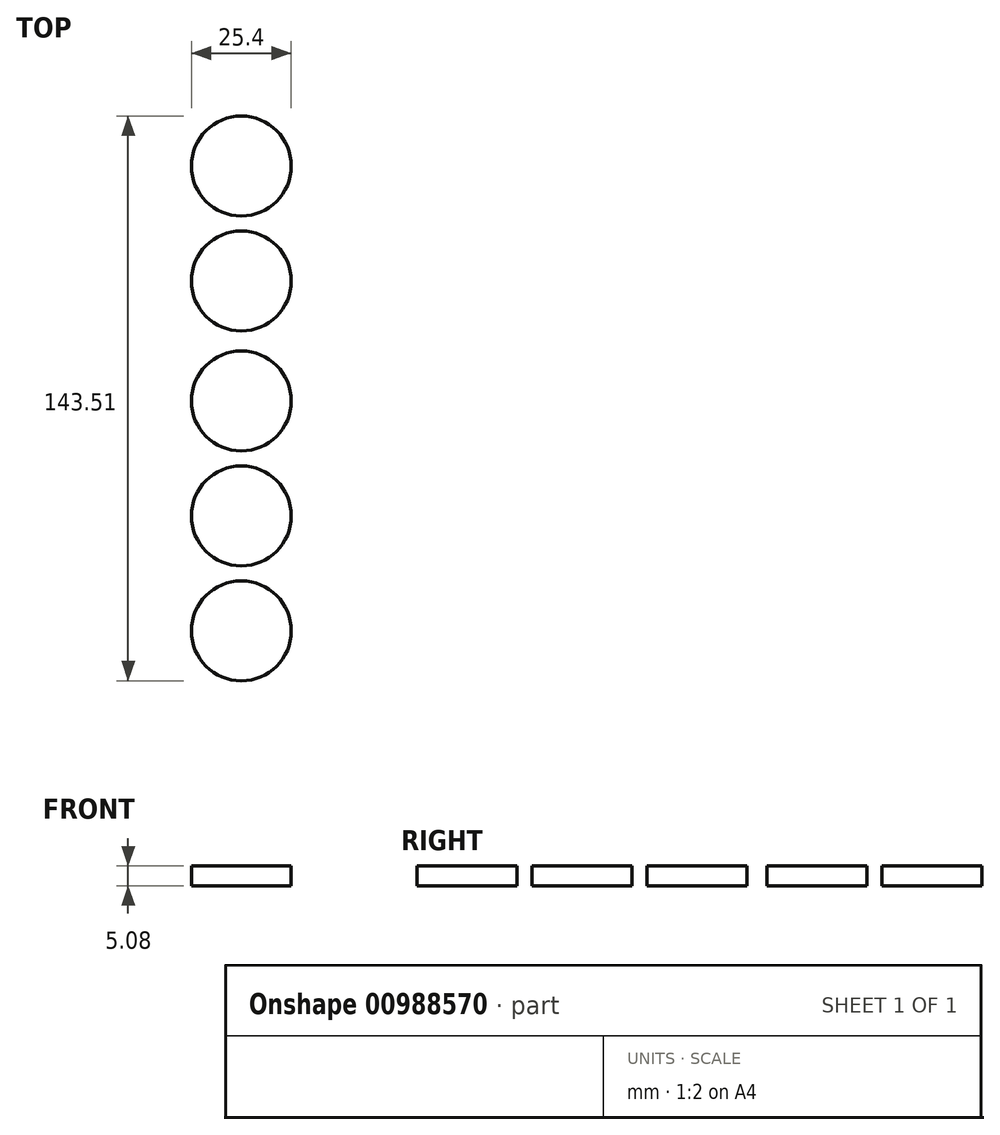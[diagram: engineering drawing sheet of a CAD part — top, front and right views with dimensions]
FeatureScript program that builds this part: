
annotation { "Feature Type Name" : "Feature", "Feature Type Description" : "" }
export const myFeature = defineFeature(function(context is Context, id is Id, definition is map)
    precondition{}
    {
        {
            var Q0;
            Q0=qCreatedBy(makeId("Top.planeOp"),FACE);
            var sketch = newSketch(context, id + "F0", { "sketchPlane" : qUnion([Q0])});
            skLineSegment(sketch, "E0.bottom", {"start": v(63.5, 76.2) * mm, "end": v(-63.5, 76.2) * mm});
            skLineSegment(sketch, "E0.top", {"start": v(63.5, -76.2) * mm, "end": v(-63.5, -76.2) * mm});
            skLineSegment(sketch, "E0.left", {"start": v(63.5, 76.2) * mm, "end": v(63.5, -76.2) * mm});
            skLineSegment(sketch, "E0.right", {"start": v(-63.5, 76.2) * mm, "end": v(-63.5, -76.2) * mm});
            skPoint(sketch, "E0.middle", {"position": v(0, 0) * mm});
            skSolve(sketch);
        }
        {
            var Q0;
            Q0=makeQuery(id+"F0.imprint","IMPRINT",FACE,{"disambiguationData":[TD([[makeQuery(id+"F0.imprint","IMPRINT",EDGE,{"derivedFrom":sQuery(id+"F0.wireOp",EDGE,"E0.bottom")}),1.0]])]});
            extrude(context, id + "F1", {"entities" : qUnion([Q0]), "depth" : 5.08 * mm, "offsetDistance" : 25.4 * mm});
        }
        {
            var Q0;
            Q0=makeQuery(id+"F1.opExtrude","CAP_FACE",FACE,{"disambiguationData":[OSD([sQuery(id+"F0.wireOp",EDGE,"E0.bottom"),sQuery(id+"F0.wireOp",EDGE,"E0.top"),sQuery(id+"F0.wireOp",EDGE,"E0.left"),sQuery(id+"F0.wireOp",EDGE,"E0.right")])],"isStart":false});
            var sketch = newSketch(context, id + "F2", { "sketchPlane" : qUnion([Q0])});
            skLineSegment(sketch, "E1", {"start": v(-63.5, -76.2) * mm, "end": v(-38.1, -76.2) * mm});
            skLineSegment(sketch, "E2", {"start": v(-38.1, -76.2) * mm, "end": v(-38.1, 76.2) * mm});
            skLineSegment(sketch, "E3", {"start": v(-38.1, 76.2) * mm, "end": v(-38.1, 59.7) * mm});
            skCircle(sketch, "E4", {"center": v(-38.1, 59.7) * mm, "radius": 12.7 * mm});
            skLineSegment(sketch, "E5", {"start": v(-38.1, 47) * mm, "end": v(-38.1, 30.48) * mm});
            skCircle(sketch, "E6", {"center": v(-38.1, 30.48) * mm, "radius": 12.7 * mm});
            skLineSegment(sketch, "E7", {"start": v(-38.1, 17.78) * mm, "end": v(-38.1, 0) * mm});
            skCircle(sketch, "E8", {"center": v(-38.1, 0) * mm, "radius": 12.7 * mm});
            skLineSegment(sketch, "E9", {"start": v(-38.1, -12.7) * mm, "end": v(-38.1, -29.2) * mm});
            skCircle(sketch, "E10", {"center": v(-38.1, -29.2) * mm, "radius": 12.7 * mm});
            skLineSegment(sketch, "E11", {"start": v(-38.1, -41.9) * mm, "end": v(-38.1, -58.42) * mm});
            skCircle(sketch, "E12", {"center": v(-38.1, -58.42) * mm, "radius": 12.7 * mm});
            skSolve(sketch);
        }
        {
            var Q0;
            {var subQ0=sQuery(id+"F2.wireOp",EDGE,"E11");var subQ1=sQuery(id+"F2.wireOp",EDGE,"E2");var subQ2=makeQuery(id+"F2.imprint","INTERSECT",VERTEX,{"derivedFrom":[subQ1,subQ0]});Q0=makeQuery(id+"F2.imprint","IMPRINT",FACE,{"disambiguationData":[TD([[makeQuery(id+"F2.imprint","IMPRINT",EDGE,{"disambiguationData":[TD([[subQ2,1.0]])],"derivedFrom":subQ1}),1.0]])]});}
            var Q1;
            {var subQ0=sQuery(id+"F2.wireOp",EDGE,"E11");var subQ1=sQuery(id+"F2.wireOp",EDGE,"E2");var subQ2=makeQuery(id+"F2.imprint","INTERSECT",VERTEX,{"derivedFrom":[subQ1,subQ0]});Q1=makeQuery(id+"F2.imprint","IMPRINT",FACE,{"disambiguationData":[TD([[makeQuery(id+"F2.imprint","IMPRINT",EDGE,{"disambiguationData":[TD([[subQ2,1.0]])],"derivedFrom":subQ1}),-1.0]])]});}
            var Q2;
            {var subQ0=sQuery(id+"F2.wireOp",EDGE,"E9");var subQ1=sQuery(id+"F2.wireOp",EDGE,"E2");var subQ2=makeQuery(id+"F2.imprint","INTERSECT",VERTEX,{"derivedFrom":[subQ1,subQ0]});Q2=makeQuery(id+"F2.imprint","IMPRINT",FACE,{"disambiguationData":[TD([[makeQuery(id+"F2.imprint","IMPRINT",EDGE,{"disambiguationData":[TD([[subQ2,1.0]])],"derivedFrom":subQ0}),-1.0]])]});}
            var Q3;
            {var subQ0=sQuery(id+"F2.wireOp",EDGE,"E9");var subQ1=sQuery(id+"F2.wireOp",EDGE,"E2");var subQ2=makeQuery(id+"F2.imprint","INTERSECT",VERTEX,{"derivedFrom":[subQ1,subQ0]});Q3=makeQuery(id+"F2.imprint","IMPRINT",FACE,{"disambiguationData":[TD([[makeQuery(id+"F2.imprint","IMPRINT",EDGE,{"disambiguationData":[TD([[subQ2,1.0]])],"derivedFrom":subQ0}),1.0]])]});}
            var Q4;
            {var subQ0=sQuery(id+"F2.wireOp",EDGE,"E7");var subQ1=sQuery(id+"F2.wireOp",EDGE,"E2");var subQ2=makeQuery(id+"F2.imprint","INTERSECT",VERTEX,{"derivedFrom":[subQ1,subQ0]});Q4=makeQuery(id+"F2.imprint","IMPRINT",FACE,{"disambiguationData":[TD([[makeQuery(id+"F2.imprint","IMPRINT",EDGE,{"disambiguationData":[TD([[subQ2,1.0]])],"derivedFrom":subQ0}),1.0]])]});}
            var Q5;
            {var subQ0=sQuery(id+"F2.wireOp",EDGE,"E7");var subQ1=sQuery(id+"F2.wireOp",EDGE,"E2");var subQ2=makeQuery(id+"F2.imprint","INTERSECT",VERTEX,{"derivedFrom":[subQ1,subQ0]});Q5=makeQuery(id+"F2.imprint","IMPRINT",FACE,{"disambiguationData":[TD([[makeQuery(id+"F2.imprint","IMPRINT",EDGE,{"disambiguationData":[TD([[subQ2,1.0]])],"derivedFrom":subQ0}),-1.0]])]});}
            var Q6;
            {var subQ0=sQuery(id+"F2.wireOp",EDGE,"E5");var subQ1=sQuery(id+"F2.wireOp",EDGE,"E2");var subQ2=makeQuery(id+"F2.imprint","INTERSECT",VERTEX,{"derivedFrom":[subQ1,subQ0]});Q6=makeQuery(id+"F2.imprint","IMPRINT",FACE,{"disambiguationData":[TD([[makeQuery(id+"F2.imprint","IMPRINT",EDGE,{"disambiguationData":[TD([[subQ2,1.0]])],"derivedFrom":subQ0}),1.0]])]});}
            var Q7;
            {var subQ0=sQuery(id+"F2.wireOp",EDGE,"E5");var subQ1=sQuery(id+"F2.wireOp",EDGE,"E2");var subQ2=makeQuery(id+"F2.imprint","INTERSECT",VERTEX,{"derivedFrom":[subQ1,subQ0]});Q7=makeQuery(id+"F2.imprint","IMPRINT",FACE,{"disambiguationData":[TD([[makeQuery(id+"F2.imprint","IMPRINT",EDGE,{"disambiguationData":[TD([[subQ2,1.0]])],"derivedFrom":subQ0}),-1.0]])]});}
            var Q8;
            {var subQ0=sQuery(id+"F2.wireOp",EDGE,"E3");var subQ1=sQuery(id+"F2.wireOp",EDGE,"E2");var subQ2=makeQuery(id+"F2.imprint","INTERSECT",VERTEX,{"derivedFrom":[subQ1,subQ0]});Q8=makeQuery(id+"F2.imprint","IMPRINT",FACE,{"disambiguationData":[TD([[makeQuery(id+"F2.imprint","IMPRINT",EDGE,{"disambiguationData":[TD([[subQ2,1.0]])],"derivedFrom":subQ0}),1.0]])]});}
            var Q9;
            {var subQ0=sQuery(id+"F2.wireOp",EDGE,"E3");var subQ1=sQuery(id+"F2.wireOp",EDGE,"E2");var subQ2=makeQuery(id+"F2.imprint","INTERSECT",VERTEX,{"derivedFrom":[subQ1,subQ0]});Q9=makeQuery(id+"F2.imprint","IMPRINT",FACE,{"disambiguationData":[TD([[makeQuery(id+"F2.imprint","IMPRINT",EDGE,{"disambiguationData":[TD([[subQ2,1.0]])],"derivedFrom":subQ0}),-1.0]])]});}
            extrude(context, id + "F3", {"entities" : qUnion([Q0, Q1, Q2, Q3, Q4, Q5, Q6, Q7, Q8, Q9]), "operationType" : NewBodyOperationType.REMOVE, "oppositeDirection" : true, "depth" : 7.62 * mm, "offsetDistance" : 25.4 * mm});
        }
    });
